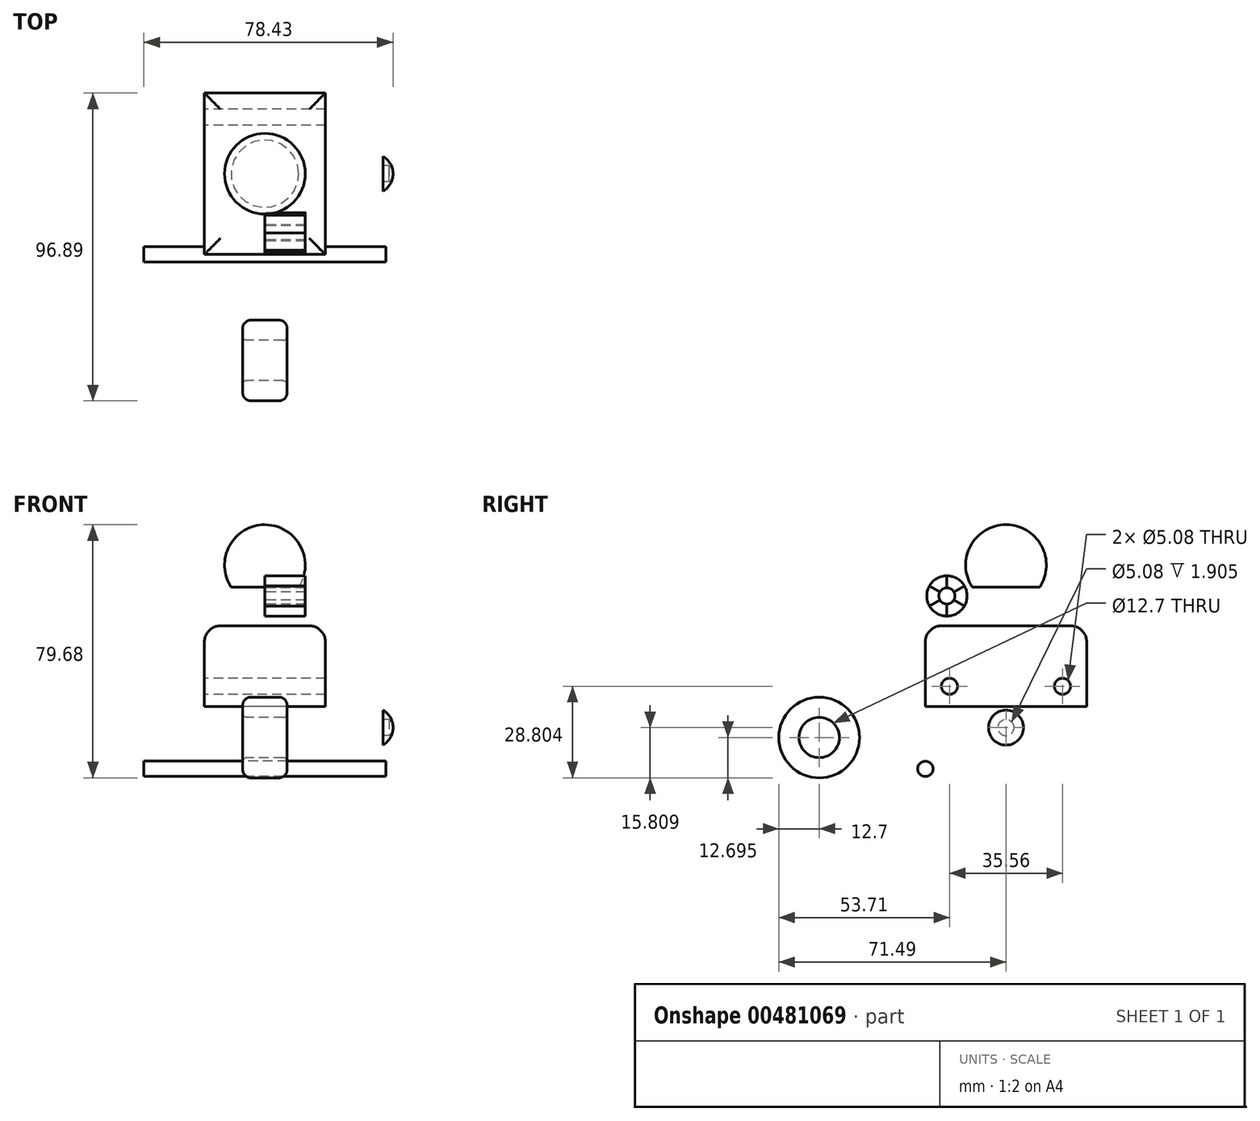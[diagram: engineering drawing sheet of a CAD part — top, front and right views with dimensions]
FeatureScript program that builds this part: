
annotation { "Feature Type Name" : "Feature", "Feature Type Description" : "" }
export const myFeature = defineFeature(function(context is Context, id is Id, definition is map)
    precondition{}
    {
        {
            var Q0;
            Q0=qCreatedBy(makeId("Front.planeOp"),FACE);
            var sketch = newSketch(context, id + "F0", { "sketchPlane" : qUnion([Q0])});
            skLineSegment(sketch, "E0.bottom", {"start": v(10.64, -6.94) * mm, "end": v(-10.63, -6.94) * mm});
            skPoint(sketch, "E0.middle", {"position": v(0, 0) * mm});
            skArc(sketch, "E1", {"start": v(-10.63, -6.94) * mm, "mid": v(0, 12.7) * mm, "end": v(10.64, -6.94) * mm});
            skLineSegment(sketch, "E2", {"start": v(0, 12.7) * mm, "end": v(0, -6.94) * mm});
            skPoint(sketch, "E0.right.end.orphan", {"position": v(-10.64, 6.94) * mm});
            skPoint(sketch, "E0.left.end.orphan", {"position": v(10.63, 6.94) * mm});
            skArc(sketch, "E3", {"start": v(40.33, -51.17) * mm, "mid": v(39.48, -48) * mm, "end": v(37.16, -45.67) * mm});
            skLineSegment(sketch, "E4", {"start": v(37.16, -51.17) * mm, "end": v(40.33, -51.17) * mm});
            skLineSegment(sketch, "E5", {"start": v(37.16, -45.67) * mm, "end": v(37.16, -51.17) * mm});
            skFitSpline(sketch, "E6", {"points": [v(-25.1, 5.76) * mm, v(-30.11, 9.73) * mm, v(-29.13, 16.05) * mm, v(-36.21, 19.57) * mm, v(-37.65, 24.76) * mm, v(-41.77, 26.65) * mm], "startDerivative": vector(-35.24, 14.87) * mm, "endDerivative": vector(-30.19, 5.57) * mm});
            skSolve(sketch);
        }
        {
            var Q0;
            {var subQ3=sQuery(id+"F0.wireOp",EDGE,"E2");Q0=makeQuery(id+"F0.imprint","IMPRINT",FACE,{"disambiguationData":[TD([[makeQuery(id+"F0.imprint","IMPRINT",EDGE,{"derivedFrom":subQ3}),1.0]])]});}
            var Q1;
            Q1=sQuery(id+"F0.wireOp",EDGE,"E2");
            revolve(context, id + "F1", {"entities" : qUnion([Q0]), "axis" : qUnion([Q1]), "revolveType" : RevolveType.FULL});
        }
        {
            var Q0;
            Q0=qCreatedBy(makeId("Right.planeOp"),FACE);
            var sketch = newSketch(context, id + "F2", { "sketchPlane" : qUnion([Q0])});
            skLineSegment(sketch, "E7.bottom", {"start": v(25.4, -44.53) * mm, "end": v(-25.4, -44.53) * mm});
            skLineSegment(sketch, "E7.top", {"start": v(25.4, -19.13) * mm, "end": v(-25.4, -19.13) * mm});
            skLineSegment(sketch, "E7.left", {"start": v(25.4, -44.53) * mm, "end": v(25.4, -19.13) * mm});
            skLineSegment(sketch, "E7.right", {"start": v(-25.4, -44.53) * mm, "end": v(-25.4, -19.13) * mm});
            skPoint(sketch, "E7.middle", {"position": v(0, -31.83) * mm});
            skCircle(sketch, "E8", {"center": v(-58.8, -54.28) * mm, "radius": 6.35 * mm});
            skCircle(sketch, "E9", {"center": v(-58.8, -54.28) * mm, "radius": 12.7 * mm});
            skCircle(sketch, "E10", {"center": v(-17.78, -38.18) * mm, "radius": 2.54 * mm});
            skCircle(sketch, "E11", {"center": v(17.78, -38.18) * mm, "radius": 2.54 * mm});
            skSolve(sketch);
        }
        {
            var Q0;
            Q0=makeQuery(id+"F2.imprint","IMPRINT",FACE,{"disambiguationData":[TD([[makeQuery(id+"F2.imprint","IMPRINT",EDGE,{"derivedFrom":sQuery(id+"F2.wireOp",EDGE,"E7.bottom")}),-1.0]])]});
            extrude(context, id + "F3", {"entities" : qUnion([Q0]), "endBound" : BoundingType.SYMMETRIC, "depth" : 38.1 * mm});
        }
        {
            var Q0;
            Q0=makeQuery(id+"F3.opExtrude","SWEPT_EDGE",EDGE,{"disambiguationData":[OSD([sQuery(id+"F2.wireOp",EDGE,"E7.top"),sQuery(id+"F2.wireOp",EDGE,"E7.right")])]});
            var Q1;
            Q1=makeQuery(id+"F3.opExtrude","SWEPT_EDGE",EDGE,{"disambiguationData":[OSD([sQuery(id+"F2.wireOp",EDGE,"E7.top"),sQuery(id+"F2.wireOp",EDGE,"E7.left")])]});
            var Q2;
            Q2=makeQuery(id+"F3.opExtrude","CAP_EDGE",EDGE,{"disambiguationData":[OSD([sQuery(id+"F2.wireOp",EDGE,"E7.top")])],"isStart":false});
            var Q3;
            Q3=makeQuery(id+"F3.opExtrude","CAP_EDGE",EDGE,{"disambiguationData":[OSD([sQuery(id+"F2.wireOp",EDGE,"E7.top")])],"isStart":true});
            fillet(context, id + "F4", {"entities" : qUnion([Q0, Q1, Q2, Q3]), "radius" : 5.08 * mm, "tangentPropagation" : true, "allowEdgeOverflow" : false});
        }
        {
            var Q0;
            Q0=qCreatedBy(makeId("Right.planeOp"),FACE);
            var sketch = newSketch(context, id + "F5", { "sketchPlane" : qUnion([Q0])});
            skCircle(sketch, "E12", {"center": v(-18.6, -9.72) * mm, "radius": 6.35 * mm});
            skLineSegment(sketch, "E13", {"start": v(-18.6, -3.37) * mm, "end": v(-18.6, -16.07) * mm});
            skLineSegment(sketch, "E14", {"start": v(-24.1, -6.56) * mm, "end": v(-13.1, -12.9) * mm});
            skLineSegment(sketch, "E15", {"start": v(-13.1, -6.53) * mm, "end": v(-24.1, -12.88) * mm});
            skCircle(sketch, "E16", {"center": v(-25.38, -64.16) * mm, "radius": 2.41 * mm});
            skCircle(sketch, "E17", {"center": v(-18.6, -9.72) * mm, "radius": 2.54 * mm});
            skCircle(sketch, "E18", {"center": v(2.12, 38.4) * mm, "radius": 1.59 * mm});
            skSolve(sketch);
        }
        {
            var Q0;
            {var subQ0=sQuery(id+"F5.wireOp",EDGE,"E13");var subQ1=sQuery(id+"F5.wireOp",EDGE,"E12");var subQ2=makeQuery(id+"F5.imprint","INTERSECT",VERTEX,{"disambiguationData":[OD(0.0)],"derivedFrom":[subQ1,subQ0]});Q0=makeQuery(id+"F5.imprint","IMPRINT",FACE,{"disambiguationData":[TD([[makeQuery(id+"F5.imprint","IMPRINT",EDGE,{"disambiguationData":[TD([[subQ2,1.0]])],"derivedFrom":subQ1}),1.0]])]});}
            extrude(context, id + "F6", {"entities" : qUnion([Q0]), "depth" : 12.7 * mm});
        }
        {
            var Q0;
            {var subQ0=sQuery(id+"F5.wireOp",EDGE,"E13");var subQ1=sQuery(id+"F5.wireOp",EDGE,"E12");var subQ2=makeQuery(id+"F5.imprint","INTERSECT",VERTEX,{"disambiguationData":[OD(0.0)],"derivedFrom":[subQ1,subQ0]});Q0=makeQuery(id+"F5.imprint","IMPRINT",FACE,{"disambiguationData":[TD([[makeQuery(id+"F5.imprint","IMPRINT",EDGE,{"disambiguationData":[TD([[subQ2,-1.0]])],"derivedFrom":subQ1}),1.0]])]});}
            extrude(context, id + "F7", {"entities" : qUnion([Q0]), "depth" : 12.7 * mm});
        }
        {
            var Q0;
            {var subQ0=sQuery(id+"F5.wireOp",EDGE,"E14");var subQ1=sQuery(id+"F5.wireOp",EDGE,"E12");var subQ2=makeQuery(id+"F5.imprint","INTERSECT",VERTEX,{"disambiguationData":[OD(0.0)],"derivedFrom":[subQ1,subQ0]});Q0=makeQuery(id+"F5.imprint","IMPRINT",FACE,{"disambiguationData":[TD([[makeQuery(id+"F5.imprint","IMPRINT",EDGE,{"disambiguationData":[TD([[subQ2,-1.0]])],"derivedFrom":subQ1}),1.0]])]});}
            extrude(context, id + "F8", {"entities" : qUnion([Q0]), "depth" : 12.7 * mm});
        }
        {
            var Q0;
            {var subQ0=sQuery(id+"F5.wireOp",EDGE,"E13");var subQ1=sQuery(id+"F5.wireOp",EDGE,"E12");var subQ2=makeQuery(id+"F5.imprint","INTERSECT",VERTEX,{"disambiguationData":[OD(1.0)],"derivedFrom":[subQ1,subQ0]});Q0=makeQuery(id+"F5.imprint","IMPRINT",FACE,{"disambiguationData":[TD([[makeQuery(id+"F5.imprint","IMPRINT",EDGE,{"disambiguationData":[TD([[subQ2,1.0]])],"derivedFrom":subQ1}),1.0]])]});}
            extrude(context, id + "F9", {"entities" : qUnion([Q0]), "depth" : 12.7 * mm});
        }
        {
            var Q0;
            {var subQ0=sQuery(id+"F5.wireOp",EDGE,"E13");var subQ1=sQuery(id+"F5.wireOp",EDGE,"E12");var subQ2=makeQuery(id+"F5.imprint","INTERSECT",VERTEX,{"disambiguationData":[OD(1.0)],"derivedFrom":[subQ1,subQ0]});Q0=makeQuery(id+"F5.imprint","IMPRINT",FACE,{"disambiguationData":[TD([[makeQuery(id+"F5.imprint","IMPRINT",EDGE,{"disambiguationData":[TD([[subQ2,-1.0]])],"derivedFrom":subQ1}),1.0]])]});}
            extrude(context, id + "F10", {"entities" : qUnion([Q0]), "depth" : 12.7 * mm});
        }
        {
            var Q0;
            {var subQ0=sQuery(id+"F5.wireOp",EDGE,"E14");var subQ1=sQuery(id+"F5.wireOp",EDGE,"E12");var subQ2=makeQuery(id+"F5.imprint","INTERSECT",VERTEX,{"disambiguationData":[OD(1.0)],"derivedFrom":[subQ1,subQ0]});Q0=makeQuery(id+"F5.imprint","IMPRINT",FACE,{"disambiguationData":[TD([[makeQuery(id+"F5.imprint","IMPRINT",EDGE,{"disambiguationData":[TD([[subQ2,-1.0]])],"derivedFrom":subQ1}),1.0]])]});}
            extrude(context, id + "F11", {"entities" : qUnion([Q0]), "depth" : 12.7 * mm});
        }
        {
            var Q0;
            Q0=makeQuery(id+"F2.imprint","IMPRINT",FACE,{"disambiguationData":[TD([[makeQuery(id+"F2.imprint","IMPRINT",EDGE,{"derivedFrom":sQuery(id+"F2.wireOp",EDGE,"E8")}),-1.0]])]});
            extrude(context, id + "F12", {"entities" : qUnion([Q0]), "endBound" : BoundingType.SYMMETRIC, "depth" : 13.97 * mm});
        }
        {
            var Q0;
            Q0=makeQuery(id+"F12.opExtrude","CAP_EDGE",EDGE,{"disambiguationData":[OSD([sQuery(id+"F2.wireOp",EDGE,"E9")])],"isStart":false});
            var Q1;
            Q1=makeQuery(id+"F12.opExtrude","CAP_EDGE",EDGE,{"disambiguationData":[OSD([sQuery(id+"F2.wireOp",EDGE,"E9")])],"isStart":true});
            fillet(context, id + "F13", {"entities" : qUnion([Q0, Q1]), "radius" : 2.54 * mm, "tangentPropagation" : true, "allowEdgeOverflow" : false});
        }
        {
            var Q0;
            Q0=makeQuery(id+"F12.opExtrude","CAP_EDGE",EDGE,{"disambiguationData":[OSD([sQuery(id+"F2.wireOp",EDGE,"E8")])],"isStart":false});
            var Q1;
            Q1=makeQuery(id+"F12.opExtrude","CAP_EDGE",EDGE,{"disambiguationData":[OSD([sQuery(id+"F2.wireOp",EDGE,"E8")])],"isStart":true});
            fillet(context, id + "F14", {"entities" : qUnion([Q0, Q1]), "radius" : 1.27 * mm, "tangentPropagation" : true, "allowEdgeOverflow" : false});
        }
        {
            var Q0;
            Q0=makeQuery(id+"F5.imprint","IMPRINT",FACE,{"disambiguationData":[TD([[makeQuery(id+"F5.imprint","IMPRINT",EDGE,{"derivedFrom":sQuery(id+"F5.wireOp",EDGE,"E16")}),1.0]])]});
            extrude(context, id + "F15", {"entities" : qUnion([Q0]), "endBound" : BoundingType.SYMMETRIC, "depth" : 76.2 * mm});
        }
        {
            var Q0;
            Q0=makeQuery(id+"F0.imprint","IMPRINT",FACE,{"disambiguationData":[TD([[makeQuery(id+"F0.imprint","IMPRINT",EDGE,{"derivedFrom":sQuery(id+"F0.wireOp",EDGE,"E3")}),1.0]])]});
            var Q1;
            Q1=sQuery(id+"F0.wireOp",EDGE,"E4");
            revolve(context, id + "F16", {"entities" : qUnion([Q0]), "axis" : qUnion([Q1]), "revolveType" : RevolveType.FULL});
        }
        {
            var Q0;
            Q0=makeQuery(id+"F16.opRevolve","SWEPT_FACE",FACE,{"disambiguationData":[OSD([sQuery(id+"F0.wireOp",EDGE,"E5")])]});
            var sketch = newSketch(context, id + "F17", { "sketchPlane" : qUnion([Q0])});
            skCircle(sketch, "E19", {"center": v(0, -51.17) * mm, "radius": 2.54 * mm});
            skSolve(sketch);
        }
        {
            var Q0;
            Q0=makeQuery(id+"F17.imprint","IMPRINT",FACE,{"disambiguationData":[TD([[makeQuery(id+"F17.imprint","IMPRINT",EDGE,{"derivedFrom":sQuery(id+"F17.wireOp",EDGE,"E19")}),1.0]])]});
            extrude(context, id + "F18", {"entities" : qUnion([Q0]), "operationType" : NewBodyOperationType.REMOVE, "oppositeDirection" : true, "depth" : 1.9 * mm});
        }
    });
